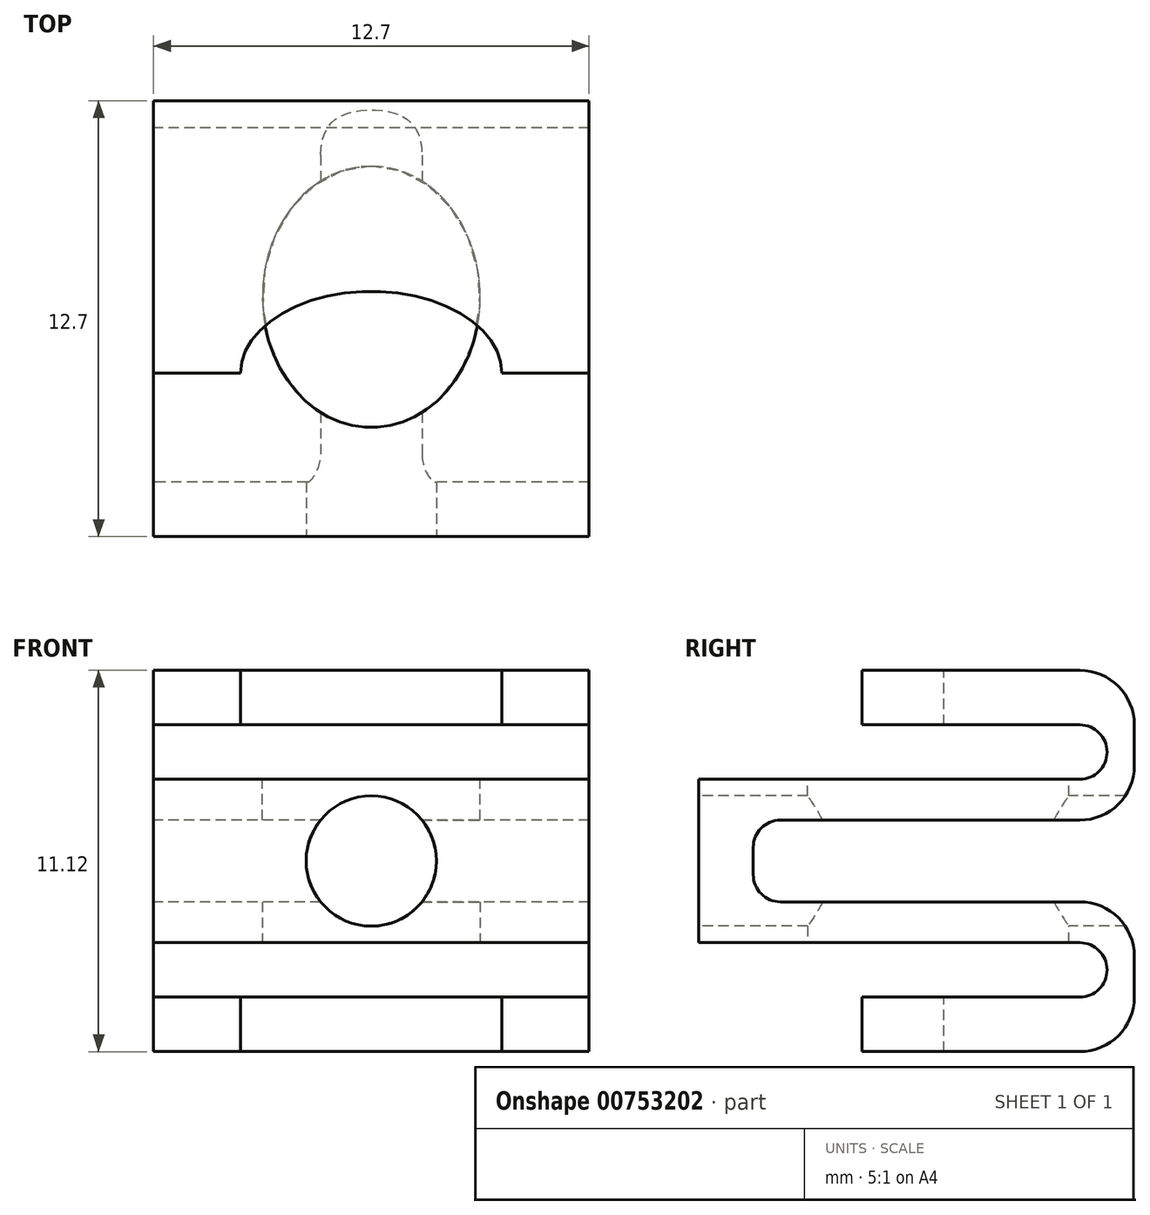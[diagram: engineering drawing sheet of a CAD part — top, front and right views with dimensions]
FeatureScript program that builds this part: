
annotation { "Feature Type Name" : "Feature", "Feature Type Description" : "" }
export const myFeature = defineFeature(function(context is Context, id is Id, definition is map)
    precondition{}
    {
        {
            var Q0;
            Q0=qCreatedBy(makeId("Right.planeOp"),FACE);
            var sketch = newSketch(context, id + "F0", { "sketchPlane" : qUnion([Q0])});
            skLineSegment(sketch, "E0.left", {"start": v(0, 2.38) * mm, "end": v(0, 0) * mm});
            skLineSegment(sketch, "E0.right", {"start": v(1.59, 0.4) * mm, "end": v(1.59, 0) * mm});
            skLineSegment(sketch, "E1.top", {"start": v(2.38, 1.2) * mm, "end": v(11.11, 1.2) * mm});
            skLineSegment(sketch, "E2.right", {"start": v(11.9, 3.18) * mm, "end": v(11.9, 3.18) * mm});
            skLineSegment(sketch, "E3.bottom", {"start": v(11.11, 5.56) * mm, "end": v(4.76, 5.56) * mm});
            skLineSegment(sketch, "E3.top", {"start": v(11.11, 3.97) * mm, "end": v(4.76, 3.97) * mm});
            skLineSegment(sketch, "E4", {"start": v(4.76, 5.56) * mm, "end": v(4.76, 3.97) * mm});
            skLineSegment(sketch, "E5", {"start": v(12.7, 2.78) * mm, "end": v(12.7, 3.97) * mm});
            skLineSegment(sketch, "E6", {"start": v(11.11, 2.38) * mm, "end": v(0, 2.38) * mm});
            skPoint(sketch, "E7.visualSharp", {"position": v(11.9, 3.97) * mm});
            skArc(sketch, "E7.filletArc", {"start": v(11.9, 3.18) * mm, "mid": v(11.67, 3.74) * mm, "end": v(11.11, 3.97) * mm});
            skPoint(sketch, "E8.visualSharp", {"position": v(11.9, 2.38) * mm});
            skArc(sketch, "E8.filletArc", {"start": v(11.11, 2.38) * mm, "mid": v(11.67, 2.61) * mm, "end": v(11.9, 3.18) * mm});
            skPoint(sketch, "E9.visualSharp", {"position": v(12.7, 5.56) * mm});
            skArc(sketch, "E9.filletArc", {"start": v(12.7, 3.97) * mm, "mid": v(12.24, 5.1) * mm, "end": v(11.11, 5.56) * mm});
            skPoint(sketch, "E10.visualSharp", {"position": v(12.7, 1.2) * mm});
            skArc(sketch, "E10.filletArc", {"start": v(11.11, 1.2) * mm, "mid": v(12.24, 1.66) * mm, "end": v(12.7, 2.78) * mm});
            skLineSegment(sketch, "E11", {"start": v(0, 0) * mm, "end": v(1.59, 0) * mm, "construction": true});
            skLineSegment(sketch, "E12.MirrorCS", {"start": v(1.59, -0.4) * mm, "end": v(1.59, 0) * mm});
            skLineSegment(sketch, "E13.MirrorCS", {"start": v(2.38, -1.2) * mm, "end": v(11.11, -1.2) * mm});
            skArc(sketch, "E14.MirrorCS", {"start": v(11.11, -1.2) * mm, "mid": v(12.24, -1.66) * mm, "end": v(12.7, -2.78) * mm});
            skLineSegment(sketch, "E15.MirrorCS", {"start": v(12.7, -2.78) * mm, "end": v(12.7, -3.97) * mm});
            skArc(sketch, "E16.MirrorCS", {"start": v(12.7, -3.97) * mm, "mid": v(12.24, -5.1) * mm, "end": v(11.11, -5.56) * mm});
            skLineSegment(sketch, "E17.MirrorCS", {"start": v(11.11, -5.56) * mm, "end": v(4.76, -5.56) * mm});
            skLineSegment(sketch, "E18.MirrorCS", {"start": v(4.76, -7.14) * mm, "end": v(4.76, -7.14) * mm});
            skLineSegment(sketch, "E19.MirrorCS", {"start": v(4.76, -5.56) * mm, "end": v(4.76, -3.97) * mm});
            skLineSegment(sketch, "E20.MirrorCS", {"start": v(11.11, -3.97) * mm, "end": v(4.76, -3.97) * mm});
            skArc(sketch, "E21.MirrorCS", {"start": v(11.9, -3.18) * mm, "mid": v(11.67, -3.74) * mm, "end": v(11.11, -3.97) * mm});
            skLineSegment(sketch, "E22.MirrorCS", {"start": v(11.11, -2.38) * mm, "end": v(0, -2.38) * mm});
            skArc(sketch, "E23.MirrorCS", {"start": v(11.11, -2.38) * mm, "mid": v(11.67, -2.61) * mm, "end": v(11.9, -3.18) * mm});
            skLineSegment(sketch, "E24.MirrorCS", {"start": v(0, -2.38) * mm, "end": v(0, 0) * mm});
            skPoint(sketch, "E25.visualSharp", {"position": v(1.59, 1.2) * mm});
            skArc(sketch, "E25.filletArc", {"start": v(2.38, 1.2) * mm, "mid": v(1.82, 0.96) * mm, "end": v(1.59, 0.4) * mm});
            skPoint(sketch, "E26.visualSharp", {"position": v(1.59, -1.2) * mm});
            skArc(sketch, "E26.filletArc", {"start": v(1.59, -0.4) * mm, "mid": v(1.82, -0.96) * mm, "end": v(2.38, -1.2) * mm});
            skPoint(sketch, "E27.visualSharp", {"position": v(0, 2.38) * mm});
            skPoint(sketch, "E28.visualSharp", {"position": v(0, -2.38) * mm});
            skPoint(sketch, "E29.top.end.orphan", {"position": v(4.76, 7.14) * mm});
            skPoint(sketch, "E30.MirrorCS.end.orphan", {"position": v(4.76, -7.14) * mm});
            skPoint(sketch, "E30.MirrorCS.start.orphan", {"position": v(4.76, -5.56) * mm});
            skSolve(sketch);
        }
        {
            var Q0;
            Q0 = qSketchRegion(id + "F0", true);
            extrude(context, id + "F1", {"entities" : qUnion([Q0]), "endBound" : BoundingType.SYMMETRIC, "depth" : 12.7 * mm, "offsetDistance" : 25.4 * mm});
        }
        {
            var Q0;
            Q0=qCreatedBy(makeId("Top.planeOp"),FACE);
            var sketch = newSketch(context, id + "F2", { "sketchPlane" : qUnion([Q0])});
            skLineSegment(sketch, "E31", {"start": v(0, 1.59) * mm, "end": v(-3.17, 1.59) * mm});
            skLineSegment(sketch, "E32", {"start": v(-3.18, 1.59) * mm, "end": v(-3.18, 14.29) * mm});
            skLineSegment(sketch, "E33", {"start": v(-3.17, 14.29) * mm, "end": v(0, 14.29) * mm});
            skLineSegment(sketch, "E34", {"start": v(0, 14.29) * mm, "end": v(0, 1.59) * mm, "construction": true});
            skLineSegment(sketch, "E35.MirrorCS", {"start": v(3.17, 14.29) * mm, "end": v(0, 14.29) * mm});
            skLineSegment(sketch, "E36.MirrorCS", {"start": v(3.18, 1.59) * mm, "end": v(3.18, 14.29) * mm});
            skLineSegment(sketch, "E37.MirrorCS", {"start": v(0, 1.59) * mm, "end": v(3.18, 1.59) * mm});
            skSolve(sketch);
        }
        {
            var Q0;
            Q0=qCreatedBy(makeId("Front.planeOp"),FACE);
            var sketch = newSketch(context, id + "F3", { "sketchPlane" : qUnion([Q0])});
            skPoint(sketch, "E38", {"position": v(0, 0) * mm});
            skSolve(sketch);
        }
        {
            var Q0;
            Q0=sQuery(id+"F3.wireOp",VERTEX,"E38");
            var Q1;
            Q1=makeQuery(id+"F1.opExtrude","SWEPT_BODY",BODY,{"disambiguationData":[OSD([sQuery(id+"F0.wireOp",EDGE,"E0.left"),sQuery(id+"F0.wireOp",EDGE,"E0.right"),sQuery(id+"F0.wireOp",EDGE,"E1.top"),sQuery(id+"F0.wireOp",EDGE,"E3.bottom"),sQuery(id+"F0.wireOp",EDGE,"E3.top"),sQuery(id+"F0.wireOp",EDGE,"E29.top"),sQuery(id+"F0.wireOp",EDGE,"E29.right"),sQuery(id+"F0.wireOp",EDGE,"E4"),sQuery(id+"F0.wireOp",EDGE,"E5"),sQuery(id+"F0.wireOp",EDGE,"E6"),sQuery(id+"F0.wireOp",EDGE,"E7.filletArc"),sQuery(id+"F0.wireOp",EDGE,"E8.filletArc"),sQuery(id+"F0.wireOp",EDGE,"E9.filletArc"),sQuery(id+"F0.wireOp",EDGE,"E10.filletArc"),sQuery(id+"F0.wireOp",EDGE,"E12.MirrorCS"),sQuery(id+"F0.wireOp",EDGE,"E13.MirrorCS"),sQuery(id+"F0.wireOp",EDGE,"E14.MirrorCS"),sQuery(id+"F0.wireOp",EDGE,"E15.MirrorCS"),sQuery(id+"F0.wireOp",EDGE,"E16.MirrorCS"),sQuery(id+"F0.wireOp",EDGE,"E17.MirrorCS"),sQuery(id+"F0.wireOp",EDGE,"E30.MirrorCS"),sQuery(id+"F0.wireOp",EDGE,"E18.MirrorCS"),sQuery(id+"F0.wireOp",EDGE,"E20.MirrorCS"),sQuery(id+"F0.wireOp",EDGE,"E21.MirrorCS"),sQuery(id+"F0.wireOp",EDGE,"E22.MirrorCS"),sQuery(id+"F0.wireOp",EDGE,"E23.MirrorCS"),sQuery(id+"F0.wireOp",EDGE,"E19.MirrorCS"),sQuery(id+"F0.wireOp",EDGE,"E24.MirrorCS"),sQuery(id+"F0.wireOp",EDGE,"E25.filletArc"),sQuery(id+"F0.wireOp",EDGE,"E26.filletArc"),sQuery(id+"F0.wireOp",EDGE,"E27.filletArc"),sQuery(id+"F0.wireOp",EDGE,"E28.filletArc")])]});
            hole(context, id + "F4", {"style" : HoleStyle.SIMPLE, "endStyle" : HoleEndStyle.THROUGH, "standardTappedOrClearance" : lookupTablePath({ "standard" : "ANSI", "fit" : "Normal (ASME)", "size" : "#6", "type" : "Clearance" }), "standardBlindInLast" : lookupTablePath({ "fit" : "Free", "standard" : "ANSI", "size" : "#6", "type" : "Clearance" }), "holeDiameter" : 3.8 * mm, "majorDiameter" : 6.35 * mm, "isTappedThrough" : true, "tappedDepth" : 12.7 * mm, "tapClearance" : 3, "locations" : qUnion([Q0]), "scope" : qUnion([Q1])});
        }
        {
            var Q0;
            Q0=makeQuery(id+"F2.imprint","IMPRINT",FACE,{"disambiguationData":[TD([[makeQuery(id+"F2.imprint","IMPRINT",EDGE,{"derivedFrom":sQuery(id+"F2.wireOp",EDGE,"E31")}),-1.0]])]});
            var sketch = newSketch(context, id + "F5", { "sketchPlane" : qUnion([Q0])});
            skPoint(sketch, "E39", {"position": v(0, 6.99) * mm});
            skEllipse(sketch, "E40", {"center": v(0, 6.99) * mm, "majorRadius": 3.81 * mm, "minorRadius": 3.18 * mm, "majorAxis": v(0, 1)});
            skSolve(sketch);
        }
        {
            var Q0;
            Q0 = qSketchRegion(id + "F5", true);
            var Q1;
            Q1=makeQuery(id+"F1.opExtrude","SWEPT_FACE",FACE,{"disambiguationData":[OSD([sQuery(id+"F0.wireOp",EDGE,"E22.MirrorCS")])]});
            var Q2;
            Q2=makeQuery(id+"F1.opExtrude","SWEPT_FACE",FACE,{"disambiguationData":[OSD([sQuery(id+"F0.wireOp",EDGE,"E6")])]});
            extrude(context, id + "F6", {"entities" : qUnion([Q0]), "operationType" : NewBodyOperationType.REMOVE, "endBound" : BoundingType.UP_TO_SURFACE, "oppositeDirection" : true, "depth" : 25.4 * mm, "endBoundEntityFace" : qUnion([Q1]), "offsetDistance" : 25.4 * mm, "hasSecondDirection" : true, "secondDirectionBound" : SecondDirectionBoundingType.UP_TO_SURFACE, "secondDirectionOppositeDirection" : false, "secondDirectionDepth" : 25.4 * mm, "secondDirectionBoundEntityFace" : qUnion([Q2])});
        }
        {
            var Q0;
            Q0=makeQuery(id+"F1.opExtrude","SWEPT_FACE",FACE,{"disambiguationData":[OSD([sQuery(id+"F0.wireOp",EDGE,"E3.bottom")])]});
            var sketch = newSketch(context, id + "F7", { "sketchPlane" : qUnion([Q0])});
            skEllipticalArc(sketch, "E41", {});
            skLineSegment(sketch, "E42", {"start": v(-3.8, 4.76) * mm, "end": v(3.81, 4.76) * mm});
            skLineSegment(sketch, "E43", {"start": v(-3.8, 7.14) * mm, "end": v(3.81, 7.14) * mm, "construction": true});
            const initialGuessF7  = {"E41": [0, 0.004762499999999999, 1, 0, 0.00381, 0.0023812500000000006, 0, 3.141592653589793]};
            skSetInitialGuess(sketch, initialGuessF7);
            skSolve(sketch);
        }
        {
            var Q0;
            Q0=makeQuery(id+"F1.opExtrude","SWEPT_FACE",FACE,{"disambiguationData":[OSD([sQuery(id+"F0.wireOp",EDGE,"E17.MirrorCS")])]});
            var sketch = newSketch(context, id + "F8", { "sketchPlane" : qUnion([Q0])});
            skEllipticalArc(sketch, "E44", {});
            skLineSegment(sketch, "E45", {"start": v(3.81, -4.76) * mm, "end": v(-3.8, -4.76) * mm});
            const initialGuessF8  = {"E44": [0, -0.004762500000000002, -1, 0, 0.00381, 0.0023812500000000006, 0, 3.141592653589793]};
            skSetInitialGuess(sketch, initialGuessF8);
            skSolve(sketch);
        }
        {
            var Q0;
            Q0 = qSketchRegion(id + "F7", true);
            extrude(context, id + "F9", {"entities" : qUnion([Q0]), "operationType" : NewBodyOperationType.REMOVE, "endBound" : BoundingType.UP_TO_NEXT, "oppositeDirection" : true, "depth" : 25.4 * mm, "offsetDistance" : 25.4 * mm});
        }
        {
            var Q0;
            Q0 = qSketchRegion(id + "F8", true);
            extrude(context, id + "F10", {"entities" : qUnion([Q0]), "operationType" : NewBodyOperationType.REMOVE, "endBound" : BoundingType.UP_TO_NEXT, "oppositeDirection" : true, "depth" : 25.4 * mm, "offsetDistance" : 25.4 * mm});
        }
    });
